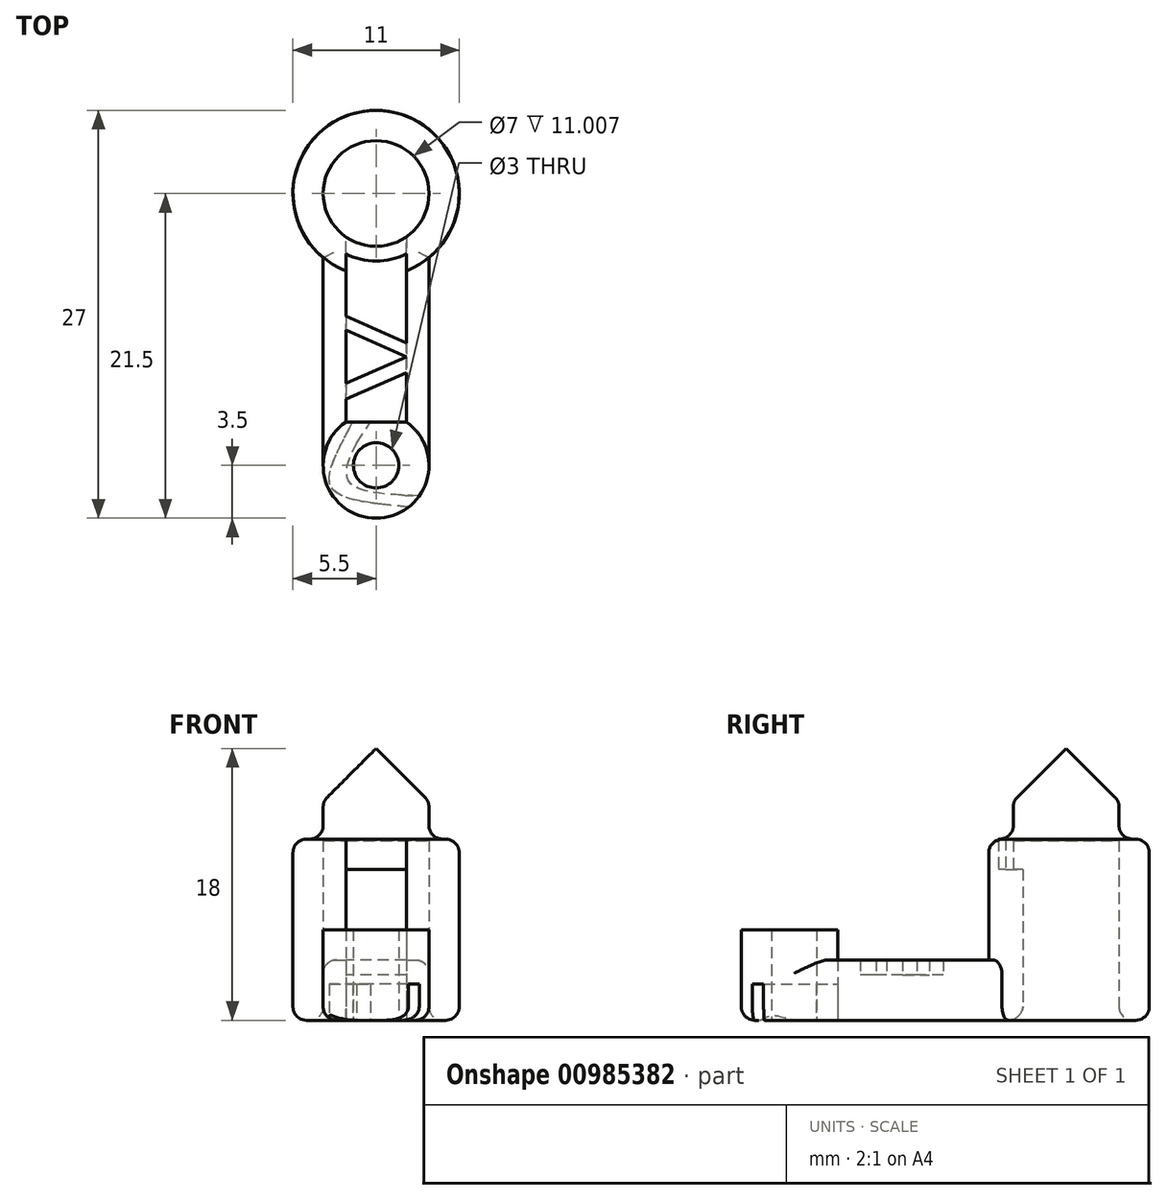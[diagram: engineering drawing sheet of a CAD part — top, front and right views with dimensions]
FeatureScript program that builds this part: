
annotation { "Feature Type Name" : "Feature", "Feature Type Description" : "" }
export const myFeature = defineFeature(function(context is Context, id is Id, definition is map)
    precondition{}
    {
        {
            var Q0;
            Q0=qCreatedBy(makeId("Top.planeOp"),FACE);
            var sketch = newSketch(context, id + "F0", { "sketchPlane" : qUnion([Q0])});
            skCircle(sketch, "E0", {"center": v(0, 18) * mm, "radius": 3.5 * mm});
            skArc(sketch, "E1", {"start": v(-0.43, 1.44) * mm, "mid": v(0, -1.5) * mm, "end": v(0.43, 1.44) * mm});
            skArc(sketch, "E2", {"start": v(5.5, 18) * mm, "mid": v(0, 23.5) * mm, "end": v(-5.5, 18) * mm});
            skPoint(sketch, "E3.orphan", {"position": v(5.5, 18) * mm});
            skArc(sketch, "E4", {"start": v(-5.5, 18) * mm, "mid": v(-4.54, 14.9) * mm, "end": v(-2, 12.88) * mm});
            skLineSegment(sketch, "E5", {"start": v(3.5, 13.76) * mm, "end": v(3.5, 0) * mm});
            skLineSegment(sketch, "E6", {"start": v(-3.5, 13.76) * mm, "end": v(-3.5, 0) * mm});
            skLineSegment(sketch, "E7.bottom", {"start": v(2, 11.5) * mm, "end": v(-2, 11.5) * mm});
            skLineSegment(sketch, "E7.top", {"start": v(2, 2.87) * mm, "end": v(-2, 2.87) * mm});
            skLineSegment(sketch, "E7.left", {"start": v(2, 11.5) * mm, "end": v(2, 2.87) * mm});
            skLineSegment(sketch, "E7.right", {"start": v(-2, 11.5) * mm, "end": v(-2, 2.87) * mm});
            skPoint(sketch, "E7.middle", {"position": v(0, 7.19) * mm});
            skLineSegment(sketch, "E8", {"start": v(-2, 9.87) * mm, "end": v(2, 8.1) * mm});
            skLineSegment(sketch, "E9", {"start": v(2, 7.19) * mm, "end": v(-2, 8.95) * mm});
            skLineSegment(sketch, "E10", {"start": v(2, 7.19) * mm, "end": v(-2, 5.42) * mm});
            skLineSegment(sketch, "E11", {"start": v(2, 6.14) * mm, "end": v(-2, 4.37) * mm});
            skLineSegment(sketch, "E12", {"start": v(2, 2.87) * mm, "end": v(2, 2.87) * mm});
            skLineSegment(sketch, "E13", {"start": v(-2, 2.87) * mm, "end": v(-2, 2.87) * mm});
            skLineSegment(sketch, "E14", {"start": v(2, 11.5) * mm, "end": v(2, 12.88) * mm});
            skLineSegment(sketch, "E15", {"start": v(-2, 11.5) * mm, "end": v(-2, 12.88) * mm});
            skLineSegment(sketch, "E16", {"start": v(2, 12.88) * mm, "end": v(2, 15.13) * mm});
            skLineSegment(sketch, "E17", {"start": v(-2, 12.88) * mm, "end": v(-2, 15.13) * mm});
            skArc(sketch, "E18.trimOffspring", {"start": v(2, 12.88) * mm, "mid": v(4.54, 14.9) * mm, "end": v(5.5, 18) * mm});
            skArc(sketch, "E19.trimOffspring", {"start": v(-2, 2.87) * mm, "mid": v(0, -3.5) * mm, "end": v(2, 2.87) * mm});
            skFitSpline(sketch, "E20", {"points": [v(2.86, -2.02) * mm, v(-1.76, -1.1) * mm, v(-1.28, 1.46) * mm], "startDerivative": vector(-10.86, 0.47) * mm, "endDerivative": vector(3.84, 7.12) * mm});
            skLineSegment(sketch, "E21", {"start": v(-1.28, 1.46) * mm, "end": v(-0.37, 2.87) * mm});
            skFitSpline(sketch, "E22", {"points": [v(2.14, -2.77) * mm, v(-2.96, -1.44) * mm, v(-1.54, 2.87) * mm], "startDerivative": vector(-12.8, 1.4) * mm, "endDerivative": vector(5.7, 11.16) * mm});
            skArc(sketch, "E23", {"start": v(0.43, 1.44) * mm, "mid": v(0, 1.5) * mm, "end": v(-0.43, 1.44) * mm});
            skArc(sketch, "E24", {"start": v(-2, 14) * mm, "mid": v(0, 13.53) * mm, "end": v(2, 14) * mm});
            skSolve(sketch);
        }
        {
            var Q0;
            {var subQ6=sQuery(id+"F0.wireOp",EDGE,"E16");Q0=makeQuery(id+"F0.imprint","IMPRINT",FACE,{"disambiguationData":[TD([[makeQuery(id+"F0.imprint","IMPRINT",EDGE,{"derivedFrom":subQ6}),-1.0]])]});}
            extrude(context, id + "F1", {"entities" : qUnion([Q0]), "depth" : 12 * mm, "offsetDistance" : 25 * mm});
        }
        {
            var Q0;
            Q0=makeQuery(id+"F0.imprint","IMPRINT",FACE,{"disambiguationData":[TD([[makeQuery(id+"F0.imprint","IMPRINT",EDGE,{"derivedFrom":sQuery(id+"F0.wireOp",EDGE,"E1")}),-1.0]])]});
            var Q1;
            {var subQ3=sQuery(id+"F0.wireOp",EDGE,"E22");Q1=makeQuery(id+"F0.imprint","IMPRINT",FACE,{"disambiguationData":[TD([[makeQuery(id+"F0.imprint","IMPRINT",EDGE,{"derivedFrom":subQ3}),1.0]])]});}
            extrude(context, id + "F2", {"entities" : qUnion([Q0, Q1]), "depth" : 6 * mm, "offsetDistance" : 25 * mm});
        }
        {
            var Q0;
            {var subQ0=sQuery(id+"F0.wireOp",EDGE,"E5");Q0=makeQuery(id+"F0.imprint","IMPRINT",FACE,{"disambiguationData":[TD([[makeQuery(id+"F0.imprint","IMPRINT",EDGE,{"derivedFrom":subQ0}),-1.0]])]});}
            var Q1;
            {var subQ5=sQuery(id+"F0.wireOp",EDGE,"E6");Q1=makeQuery(id+"F0.imprint","IMPRINT",FACE,{"disambiguationData":[TD([[makeQuery(id+"F0.imprint","IMPRINT",EDGE,{"derivedFrom":subQ5}),1.0]])]});}
            extrude(context, id + "F3", {"entities" : qUnion([Q0, Q1]), "operationType" : NewBodyOperationType.ADD, "depth" : 4 * mm, "offsetDistance" : 25 * mm});
        }
        {
            var Q0;
            {var subQ0=sQuery(id+"F0.wireOp",EDGE,"t8vcd0od-Q5oX-dSly-AOnn-WLLdnDnognq7");Q0=makeQuery(id+"F0.imprint","IMPRINT",FACE,{"disambiguationData":[TD([[makeQuery(id+"F0.imprint","IMPRINT",EDGE,{"derivedFrom":subQ0}),1.0]])]});}
            var Q1;
            {var subQ0=sQuery(id+"F0.wireOp",EDGE,"IIhoLUfB-7Anf-gRkd-r3PI-RIw168ApgjO5");Q1=makeQuery(id+"F0.imprint","IMPRINT",FACE,{"disambiguationData":[TD([[makeQuery(id+"F0.imprint","IMPRINT",EDGE,{"derivedFrom":subQ0}),-1.0]])]});}
            var Q2;
            {var subQ0=sQuery(id+"F0.wireOp",EDGE,"obxHUpex-AfBQ-ksu6-tvqv-lt50Td6Xnom8");Q2=makeQuery(id+"F0.imprint","IMPRINT",FACE,{"disambiguationData":[TD([[makeQuery(id+"F0.imprint","IMPRINT",EDGE,{"derivedFrom":subQ0}),-1.0]])]});}
            var Q3;
            {var subQ0=sQuery(id+"F0.wireOp",EDGE,"E8");Q3=makeQuery(id+"F0.imprint","IMPRINT",FACE,{"disambiguationData":[TD([[makeQuery(id+"F0.imprint","IMPRINT",EDGE,{"derivedFrom":subQ0}),-1.0]])]});}
            var Q4;
            {var subQ0=sQuery(id+"F0.wireOp",EDGE,"B4xm6HP1-7AOj-g9Be-ZZEb-mDNHuuVnzBqk");Q4=makeQuery(id+"F0.imprint","IMPRINT",FACE,{"disambiguationData":[TD([[makeQuery(id+"F0.imprint","IMPRINT",EDGE,{"derivedFrom":subQ0}),-1.0]])]});}
            var Q5;
            {var subQ5=sQuery(id+"F0.wireOp",EDGE,"qx0ybP9T-TfWC-urit-lL5r-SpVVSMcNtTrG");Q5=makeQuery(id+"F0.imprint","IMPRINT",FACE,{"disambiguationData":[TD([[makeQuery(id+"F0.imprint","IMPRINT",EDGE,{"derivedFrom":subQ5}),1.0]])]});}
            var Q6;
            {var subQ0=sQuery(id+"F0.wireOp",EDGE,"E10");Q6=makeQuery(id+"F0.imprint","IMPRINT",FACE,{"disambiguationData":[TD([[makeQuery(id+"F0.imprint","IMPRINT",EDGE,{"derivedFrom":subQ0}),1.0]])]});}
            extrude(context, id + "F4", {"entities" : qUnion([Q0, Q1, Q2, Q3, Q4, Q5, Q6]), "operationType" : NewBodyOperationType.ADD, "depth" : 4 * mm, "offsetDistance" : 25 * mm, "hasSecondDirection" : true, "secondDirectionOppositeDirection" : false, "secondDirectionDepth" : 3 * mm});
        }
        {
            var Q0;
            {var subQ0=sQuery(id+"F0.wireOp",EDGE,"E0");var subQ1=makeQuery(id+"F0.imprint","INTERSECT",VERTEX,{"derivedFrom":[subQ0,sQuery(id+"F0.wireOp",EDGE,"E16")]});Q0=makeQuery(id+"F0.imprint","IMPRINT",FACE,{"disambiguationData":[TD([[makeQuery(id+"F0.imprint","IMPRINT",EDGE,{"disambiguationData":[TD([[subQ1,1.0]])],"derivedFrom":subQ0}),1.0]])]});}
            extrude(context, id + "F5", {"entities" : qUnion([Q0]), "operationType" : NewBodyOperationType.ADD, "depth" : 18 * mm, "offsetDistance" : 25 * mm, "hasSecondDirection" : true, "secondDirectionOppositeDirection" : false, "secondDirectionDepth" : 11.9 * mm});
        }
        {
            var Q0;
            {var subQ1=sQuery(id+"F0.wireOp",EDGE,"E20");Q0=makeQuery(id+"F0.imprint","IMPRINT",FACE,{"disambiguationData":[TD([[makeQuery(id+"F0.imprint","IMPRINT",EDGE,{"derivedFrom":subQ1}),1.0]])]});}
            extrude(context, id + "F6", {"entities" : qUnion([Q0]), "operationType" : NewBodyOperationType.ADD, "depth" : 6 * mm, "offsetDistance" : 25 * mm, "hasSecondDirection" : true, "secondDirectionOppositeDirection" : false, "secondDirectionDepth" : 2.4 * mm});
        }
        {
            var Q0;
            {var subQ5=sQuery(id+"F0.wireOp",EDGE,"E24");Q0=makeQuery(id+"F0.imprint","IMPRINT",FACE,{"disambiguationData":[TD([[makeQuery(id+"F0.imprint","IMPRINT",EDGE,{"derivedFrom":subQ5}),1.0]])]});}
            extrude(context, id + "F7", {"entities" : qUnion([Q0]), "operationType" : NewBodyOperationType.ADD, "depth" : 12 * mm, "offsetDistance" : 25 * mm, "hasSecondDirection" : true, "secondDirectionOppositeDirection" : false, "secondDirectionDepth" : 10 * mm});
        }
        {
            var Q0;
            Q0=makeQuery(id+"F5.opExtrude","CAP_EDGE",EDGE,{"disambiguationData":[OSD([sQuery(id+"F0.wireOp",EDGE,"E0")])],"isStart":false});
            chamfer(context, id + "F8", {"entities" : qUnion([Q0]), "width" : 3.5 * mm, "tangentPropagation" : true});
        }
        {
            var Q0;
            Q0=makeQuery(id+"F5.opExtrude","SWEPT_FACE",FACE,{"disambiguationData":[OSD([sQuery(id+"F0.wireOp",EDGE,"E0")])]});
            var Q1;
            Q1=makeQuery(id+"F1.opExtrude","CAP_EDGE",EDGE,{"disambiguationData":[OSD([sQuery(id+"F0.wireOp",EDGE,"E2"),sQuery(id+"F0.wireOp",EDGE,"E4"),sQuery(id+"F0.wireOp",EDGE,"E18.trimOffspring")])],"isStart":false});
            var Q2;
            Q2=makeQuery(id+"F3.opExtrude","CAP_EDGE",EDGE,{"disambiguationData":[OSD([sQuery(id+"F0.wireOp",EDGE,"E5")])],"isStart":false});
            var Q3;
            Q3=makeQuery(id+"F3.opExtrude","CAP_EDGE",EDGE,{"disambiguationData":[OSD([sQuery(id+"F0.wireOp",EDGE,"E5")])],"isStart":true});
            var Q4;
            Q4=makeQuery(id+"F3.opExtrude","CAP_EDGE",EDGE,{"disambiguationData":[OSD([sQuery(id+"F0.wireOp",EDGE,"E6")])],"isStart":false});
            var Q5;
            Q5=makeQuery(id+"F3.opExtrude","CAP_EDGE",EDGE,{"disambiguationData":[OSD([sQuery(id+"F0.wireOp",EDGE,"E6")])],"isStart":true});
            var Q6;
            Q6=makeQuery(id+"F1.opExtrude","CAP_EDGE",EDGE,{"disambiguationData":[OSD([sQuery(id+"F0.wireOp",EDGE,"E0")])],"isStart":true});
            var Q7;
            Q7=makeQuery(id+"F1.opExtrude","CAP_EDGE",EDGE,{"disambiguationData":[OSD([sQuery(id+"F0.wireOp",EDGE,"E2"),sQuery(id+"F0.wireOp",EDGE,"E4"),sQuery(id+"F0.wireOp",EDGE,"E18.trimOffspring")])],"isStart":true});
            fillet(context, id + "F9", {"entities" : qUnion([Q0, Q1, Q2, Q3, Q4, Q5, Q6, Q7]), "radius" : 0.9 * mm, "tangentPropagation" : true, "allowEdgeOverflow" : false});
        }
    });
